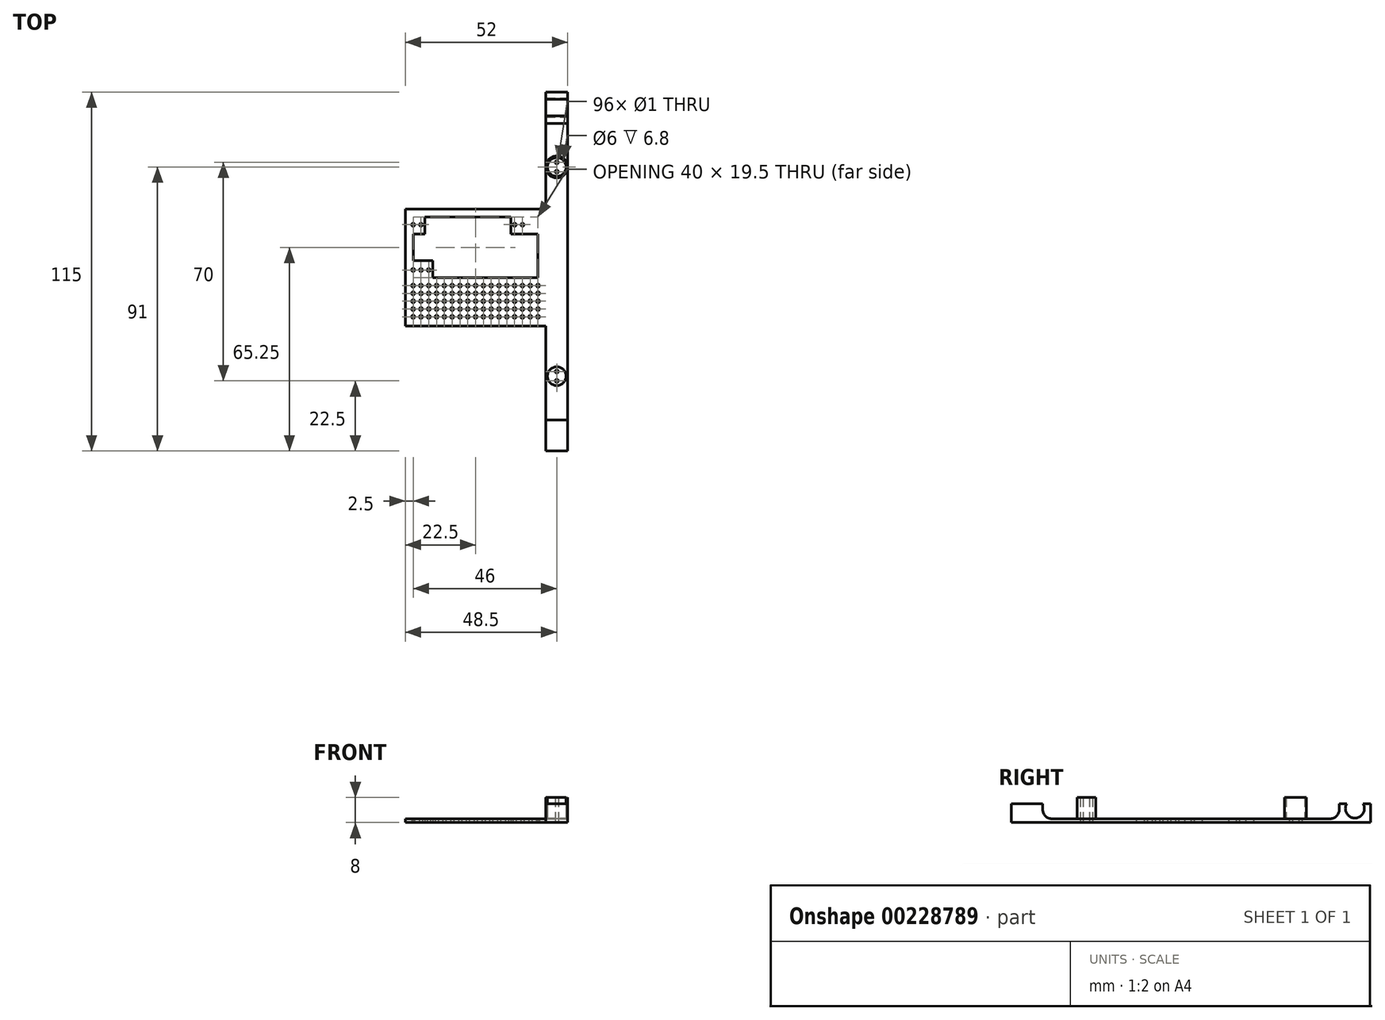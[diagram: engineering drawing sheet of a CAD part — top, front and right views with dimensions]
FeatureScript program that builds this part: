
annotation { "Feature Type Name" : "Feature", "Feature Type Description" : "" }
export const myFeature = defineFeature(function(context is Context, id is Id, definition is map)
    precondition{}
    {
        {
            var Q0;
            Q0=qCreatedBy(makeId("Top.planeOp"),FACE);
            var sketch = newSketch(context, id + "F0", { "sketchPlane" : qUnion([Q0])});
            skLineSegment(sketch, "E0.bottom", {"start": v(-22.5, 17.5) * mm, "end": v(22.5, 17.5) * mm});
            skLineSegment(sketch, "E0.top", {"start": v(-22.5, -17.5) * mm, "end": v(22.5, -17.5) * mm});
            skLineSegment(sketch, "E0.left", {"start": v(-22.5, 17.5) * mm, "end": v(-22.5, -17.5) * mm});
            skLineSegment(sketch, "E0.right", {"start": v(22.5, 17.5) * mm, "end": v(22.5, -17.5) * mm});
            skPoint(sketch, "E0.middle", {"position": v(0, 0) * mm});
            skCircle(sketch, "E1", {"center": v(-20, 15) * mm, "radius": 0.5 * mm});
            skLineSegment(sketch, "E2", {"start": v(-20, 15) * mm, "end": v(22.5, 15) * mm, "construction": true});
            skCircle(sketch, "E3.0.1.1", {"center": v(-20, 0.5) * mm, "radius": 0.5 * mm});
            skCircle(sketch, "E3.1.0.1", {"center": v(-17.5, 15) * mm, "radius": 0.5 * mm});
            skCircle(sketch, "E3.1.1.1", {"center": v(-17.5, 0.5) * mm, "radius": 0.5 * mm});
            skCircle(sketch, "E3.2.0.1", {"center": v(-15, 15) * mm, "radius": 0.5 * mm});
            skCircle(sketch, "E3.2.1.1", {"center": v(-15, 0.5) * mm, "radius": 0.5 * mm});
            skCircle(sketch, "E3.3.0.1", {"center": v(-12.5, 15) * mm, "radius": 0.5 * mm});
            skCircle(sketch, "E3.3.1.1", {"center": v(-12.5, 0.5) * mm, "radius": 0.5 * mm});
            skCircle(sketch, "E3.4.0.1", {"center": v(-10, 15) * mm, "radius": 0.5 * mm});
            skCircle(sketch, "E3.4.1.1", {"center": v(-10, 0.5) * mm, "radius": 0.5 * mm});
            skCircle(sketch, "E3.5.0.1", {"center": v(-7.5, 15) * mm, "radius": 0.5 * mm});
            skCircle(sketch, "E3.5.1.1", {"center": v(-7.5, 0.5) * mm, "radius": 0.5 * mm});
            skCircle(sketch, "E3.6.0.1", {"center": v(-5, 15) * mm, "radius": 0.5 * mm});
            skCircle(sketch, "E3.6.1.1", {"center": v(-5, 0.5) * mm, "radius": 0.5 * mm});
            skCircle(sketch, "E3.7.0.1", {"center": v(-2.5, 15) * mm, "radius": 0.5 * mm});
            skCircle(sketch, "E3.7.1.1", {"center": v(-2.5, 0.5) * mm, "radius": 0.5 * mm});
            skCircle(sketch, "E3.8.0.1", {"center": v(0, 15) * mm, "radius": 0.5 * mm});
            skCircle(sketch, "E3.8.1.1", {"center": v(0, 0.5) * mm, "radius": 0.5 * mm});
            skCircle(sketch, "E3.9.0.1", {"center": v(2.5, 15) * mm, "radius": 0.5 * mm});
            skCircle(sketch, "E3.9.1.1", {"center": v(2.5, 0.5) * mm, "radius": 0.5 * mm});
            skCircle(sketch, "E3.10.0.1", {"center": v(5, 15) * mm, "radius": 0.5 * mm});
            skCircle(sketch, "E3.10.1.1", {"center": v(5, 0.5) * mm, "radius": 0.5 * mm});
            skCircle(sketch, "E3.11.0.1", {"center": v(7.5, 15) * mm, "radius": 0.5 * mm});
            skCircle(sketch, "E3.11.1.1", {"center": v(7.5, 0.5) * mm, "radius": 0.5 * mm});
            skCircle(sketch, "E3.12.0.1", {"center": v(10, 15) * mm, "radius": 0.5 * mm});
            skCircle(sketch, "E3.12.1.1", {"center": v(10, 0.5) * mm, "radius": 0.5 * mm});
            skCircle(sketch, "E3.13.0.1", {"center": v(12.5, 15) * mm, "radius": 0.5 * mm});
            skCircle(sketch, "E3.13.1.1", {"center": v(12.5, 0.5) * mm, "radius": 0.5 * mm});
            skCircle(sketch, "E3.14.0.1", {"center": v(15, 15) * mm, "radius": 0.5 * mm});
            skCircle(sketch, "E3.14.1.1", {"center": v(15, 0.5) * mm, "radius": 0.5 * mm});
            skLineSegment(sketch, "E3.direction1", {"start": v(-20, 15) * mm, "end": v(-17.5, 15) * mm, "construction": true});
            skLineSegment(sketch, "E3.direction2", {"start": v(-20, 15) * mm, "end": v(-20, 0.5) * mm, "construction": true});
            skLineSegment(sketch, "E4", {"start": v(-22.5, -2) * mm, "end": v(22.5, -2) * mm, "construction": true});
            skCircle(sketch, "E5.MirrorC", {"center": v(-20, -4.5) * mm, "radius": 0.5 * mm});
            skCircle(sketch, "E6.0.1.0", {"center": v(-20, -7) * mm, "radius": 0.5 * mm});
            skCircle(sketch, "E6.0.2.0", {"center": v(-20, -9.5) * mm, "radius": 0.5 * mm});
            skCircle(sketch, "E6.0.3.0", {"center": v(-20, -12) * mm, "radius": 0.5 * mm});
            skCircle(sketch, "E6.1.0.0", {"center": v(-17.5, -4.5) * mm, "radius": 0.5 * mm});
            skCircle(sketch, "E6.1.1.0", {"center": v(-17.5, -7) * mm, "radius": 0.5 * mm});
            skCircle(sketch, "E6.1.2.0", {"center": v(-17.5, -9.5) * mm, "radius": 0.5 * mm});
            skCircle(sketch, "E6.1.3.0", {"center": v(-17.5, -12) * mm, "radius": 0.5 * mm});
            skCircle(sketch, "E6.2.0.0", {"center": v(-15, -4.5) * mm, "radius": 0.5 * mm});
            skCircle(sketch, "E6.2.1.0", {"center": v(-15, -7) * mm, "radius": 0.5 * mm});
            skCircle(sketch, "E6.2.2.0", {"center": v(-15, -9.5) * mm, "radius": 0.5 * mm});
            skCircle(sketch, "E6.2.3.0", {"center": v(-15, -12) * mm, "radius": 0.5 * mm});
            skCircle(sketch, "E6.3.0.0", {"center": v(-12.5, -4.5) * mm, "radius": 0.5 * mm});
            skCircle(sketch, "E6.3.1.0", {"center": v(-12.5, -7) * mm, "radius": 0.5 * mm});
            skCircle(sketch, "E6.3.2.0", {"center": v(-12.5, -9.5) * mm, "radius": 0.5 * mm});
            skCircle(sketch, "E6.3.3.0", {"center": v(-12.5, -12) * mm, "radius": 0.5 * mm});
            skCircle(sketch, "E6.4.0.0", {"center": v(-10, -4.5) * mm, "radius": 0.5 * mm});
            skCircle(sketch, "E6.4.1.0", {"center": v(-10, -7) * mm, "radius": 0.5 * mm});
            skCircle(sketch, "E6.4.2.0", {"center": v(-10, -9.5) * mm, "radius": 0.5 * mm});
            skCircle(sketch, "E6.4.3.0", {"center": v(-10, -12) * mm, "radius": 0.5 * mm});
            skCircle(sketch, "E6.5.0.0", {"center": v(-7.5, -4.5) * mm, "radius": 0.5 * mm});
            skCircle(sketch, "E6.5.1.0", {"center": v(-7.5, -7) * mm, "radius": 0.5 * mm});
            skCircle(sketch, "E6.5.2.0", {"center": v(-7.5, -9.5) * mm, "radius": 0.5 * mm});
            skCircle(sketch, "E6.5.3.0", {"center": v(-7.5, -12) * mm, "radius": 0.5 * mm});
            skCircle(sketch, "E6.6.0.0", {"center": v(-5, -4.5) * mm, "radius": 0.5 * mm});
            skCircle(sketch, "E6.6.1.0", {"center": v(-5, -7) * mm, "radius": 0.5 * mm});
            skCircle(sketch, "E6.6.2.0", {"center": v(-5, -9.5) * mm, "radius": 0.5 * mm});
            skCircle(sketch, "E6.6.3.0", {"center": v(-5, -12) * mm, "radius": 0.5 * mm});
            skCircle(sketch, "E6.7.0.0", {"center": v(-2.5, -4.5) * mm, "radius": 0.5 * mm});
            skCircle(sketch, "E6.7.1.0", {"center": v(-2.5, -7) * mm, "radius": 0.5 * mm});
            skCircle(sketch, "E6.7.2.0", {"center": v(-2.5, -9.5) * mm, "radius": 0.5 * mm});
            skCircle(sketch, "E6.7.3.0", {"center": v(-2.5, -12) * mm, "radius": 0.5 * mm});
            skCircle(sketch, "E6.8.0.0", {"center": v(0, -4.5) * mm, "radius": 0.5 * mm});
            skCircle(sketch, "E6.8.1.0", {"center": v(0, -7) * mm, "radius": 0.5 * mm});
            skCircle(sketch, "E6.8.2.0", {"center": v(0, -9.5) * mm, "radius": 0.5 * mm});
            skCircle(sketch, "E6.8.3.0", {"center": v(0, -12) * mm, "radius": 0.5 * mm});
            skCircle(sketch, "E6.9.0.0", {"center": v(2.5, -4.5) * mm, "radius": 0.5 * mm});
            skCircle(sketch, "E6.9.1.0", {"center": v(2.5, -7) * mm, "radius": 0.5 * mm});
            skCircle(sketch, "E6.9.2.0", {"center": v(2.5, -9.5) * mm, "radius": 0.5 * mm});
            skCircle(sketch, "E6.9.3.0", {"center": v(2.5, -12) * mm, "radius": 0.5 * mm});
            skCircle(sketch, "E6.10.0.0", {"center": v(5, -4.5) * mm, "radius": 0.5 * mm});
            skCircle(sketch, "E6.10.1.0", {"center": v(5, -7) * mm, "radius": 0.5 * mm});
            skCircle(sketch, "E6.10.2.0", {"center": v(5, -9.5) * mm, "radius": 0.5 * mm});
            skCircle(sketch, "E6.10.3.0", {"center": v(5, -12) * mm, "radius": 0.5 * mm});
            skCircle(sketch, "E6.11.0.0", {"center": v(7.5, -4.5) * mm, "radius": 0.5 * mm});
            skCircle(sketch, "E6.11.1.0", {"center": v(7.5, -7) * mm, "radius": 0.5 * mm});
            skCircle(sketch, "E6.11.2.0", {"center": v(7.5, -9.5) * mm, "radius": 0.5 * mm});
            skCircle(sketch, "E6.11.3.0", {"center": v(7.5, -12) * mm, "radius": 0.5 * mm});
            skCircle(sketch, "E6.12.0.0", {"center": v(10, -4.5) * mm, "radius": 0.5 * mm});
            skCircle(sketch, "E6.12.1.0", {"center": v(10, -7) * mm, "radius": 0.5 * mm});
            skCircle(sketch, "E6.12.2.0", {"center": v(10, -9.5) * mm, "radius": 0.5 * mm});
            skCircle(sketch, "E6.12.3.0", {"center": v(10, -12) * mm, "radius": 0.5 * mm});
            skCircle(sketch, "E6.13.0.0", {"center": v(12.5, -4.5) * mm, "radius": 0.5 * mm});
            skCircle(sketch, "E6.13.1.0", {"center": v(12.5, -7) * mm, "radius": 0.5 * mm});
            skCircle(sketch, "E6.13.2.0", {"center": v(12.5, -9.5) * mm, "radius": 0.5 * mm});
            skCircle(sketch, "E6.13.3.0", {"center": v(12.5, -12) * mm, "radius": 0.5 * mm});
            skCircle(sketch, "E6.14.0.0", {"center": v(15, -4.5) * mm, "radius": 0.5 * mm});
            skCircle(sketch, "E6.14.1.0", {"center": v(15, -7) * mm, "radius": 0.5 * mm});
            skCircle(sketch, "E6.14.2.0", {"center": v(15, -9.5) * mm, "radius": 0.5 * mm});
            skCircle(sketch, "E6.14.3.0", {"center": v(15, -12) * mm, "radius": 0.5 * mm});
            skLineSegment(sketch, "E6.direction1", {"start": v(-20, -4.5) * mm, "end": v(-17.5, -4.5) * mm, "construction": true});
            skLineSegment(sketch, "E6.direction2", {"start": v(-20, -4.5) * mm, "end": v(-20, -7) * mm, "construction": true});
            skCircle(sketch, "E7.0.15.0", {"center": v(17.5, -4.5) * mm, "radius": 0.5 * mm});
            skCircle(sketch, "E7.0.15.1", {"center": v(17.5, -7) * mm, "radius": 0.5 * mm});
            skCircle(sketch, "E7.0.15.2", {"center": v(17.5, -9.5) * mm, "radius": 0.5 * mm});
            skCircle(sketch, "E7.0.15.3", {"center": v(17.5, -12) * mm, "radius": 0.5 * mm});
            skCircle(sketch, "E8.0.16.0", {"center": v(20, -4.5) * mm, "radius": 0.5 * mm});
            skCircle(sketch, "E8.0.16.1", {"center": v(20, -7) * mm, "radius": 0.5 * mm});
            skCircle(sketch, "E8.0.16.2", {"center": v(20, -9.5) * mm, "radius": 0.5 * mm});
            skCircle(sketch, "E8.0.16.3", {"center": v(20, -12) * mm, "radius": 0.5 * mm});
            skCircle(sketch, "E9.0.0.4", {"center": v(-20, -14.5) * mm, "radius": 0.5 * mm});
            skCircle(sketch, "E9.0.1.4", {"center": v(-17.5, -14.5) * mm, "radius": 0.5 * mm});
            skCircle(sketch, "E9.0.2.4", {"center": v(-15, -14.5) * mm, "radius": 0.5 * mm});
            skCircle(sketch, "E9.0.3.4", {"center": v(-12.5, -14.5) * mm, "radius": 0.5 * mm});
            skCircle(sketch, "E9.0.4.4", {"center": v(-10, -14.5) * mm, "radius": 0.5 * mm});
            skCircle(sketch, "E9.0.5.4", {"center": v(-7.5, -14.5) * mm, "radius": 0.5 * mm});
            skCircle(sketch, "E9.0.6.4", {"center": v(-5, -14.5) * mm, "radius": 0.5 * mm});
            skCircle(sketch, "E9.0.7.4", {"center": v(-2.5, -14.5) * mm, "radius": 0.5 * mm});
            skCircle(sketch, "E9.0.8.4", {"center": v(0, -14.5) * mm, "radius": 0.5 * mm});
            skCircle(sketch, "E9.0.9.4", {"center": v(2.5, -14.5) * mm, "radius": 0.5 * mm});
            skCircle(sketch, "E9.0.10.4", {"center": v(5, -14.5) * mm, "radius": 0.5 * mm});
            skCircle(sketch, "E9.0.11.4", {"center": v(7.5, -14.5) * mm, "radius": 0.5 * mm});
            skCircle(sketch, "E9.0.12.4", {"center": v(10, -14.5) * mm, "radius": 0.5 * mm});
            skCircle(sketch, "E9.0.13.4", {"center": v(12.5, -14.5) * mm, "radius": 0.5 * mm});
            skCircle(sketch, "E9.0.14.4", {"center": v(15, -14.5) * mm, "radius": 0.5 * mm});
            skCircle(sketch, "E9.0.15.4", {"center": v(17.5, -14.5) * mm, "radius": 0.5 * mm});
            skCircle(sketch, "E9.0.16.4", {"center": v(20, -14.5) * mm, "radius": 0.5 * mm});
            skLineSegment(sketch, "E10.bottom", {"start": v(-20, 12) * mm, "end": v(20, 12) * mm});
            skLineSegment(sketch, "E10.top", {"start": v(-20, 3.5) * mm, "end": v(20, 3.5) * mm});
            skLineSegment(sketch, "E10.left", {"start": v(-20, 12) * mm, "end": v(-20, 3.5) * mm});
            skLineSegment(sketch, "E10.right", {"start": v(20, 12) * mm, "end": v(20, 3.5) * mm});
            skPoint(sketch, "E10.middle", {"position": v(0, 7.75) * mm});
            skLineSegment(sketch, "E11", {"start": v(22.5, 17.5) * mm, "end": v(22.5, 57.5) * mm});
            skLineSegment(sketch, "E12", {"start": v(22.5, 57.5) * mm, "end": v(29.5, 57.5) * mm});
            skLineSegment(sketch, "E13", {"start": v(29.5, -2) * mm, "end": v(22.5, -2) * mm, "construction": true});
            skLineSegment(sketch, "E14", {"start": v(29.5, 57.5) * mm, "end": v(29.5, -2) * mm});
            skLineSegment(sketch, "E15", {"start": v(22.5, 47.5) * mm, "end": v(29.5, 47.5) * mm});
            skLineSegment(sketch, "E16.MirrorCS", {"start": v(22.5, -47.5) * mm, "end": v(29.5, -47.5) * mm});
            skLineSegment(sketch, "E17.MirrorCS", {"start": v(29.5, -57.5) * mm, "end": v(29.5, 2) * mm});
            skLineSegment(sketch, "E18.MirrorCS", {"start": v(22.5, -17.5) * mm, "end": v(22.5, -57.5) * mm});
            skLineSegment(sketch, "E19.MirrorCS", {"start": v(22.5, -57.5) * mm, "end": v(29.5, -57.5) * mm});
            skCircle(sketch, "E20", {"center": v(26, 33.5) * mm, "radius": 3 * mm});
            skPoint(sketch, "E20.centerSnap0", {"position": v(26, 47.5) * mm});
            skCircle(sketch, "E21", {"center": v(26, 33.5) * mm, "radius": 3.5 * mm});
            skCircle(sketch, "E22.MirrorC", {"center": v(26, -33.5) * mm, "radius": 3 * mm});
            skCircle(sketch, "E23.MirrorC", {"center": v(26, -33.5) * mm, "radius": 3.5 * mm});
            skCircle(sketch, "E24", {"center": v(26, 35) * mm, "radius": 0.5 * mm});
            skCircle(sketch, "E25", {"center": v(26, 32) * mm, "radius": 0.5 * mm});
            skCircle(sketch, "E26.MirrorC", {"center": v(26, -35) * mm, "radius": 0.5 * mm});
            skCircle(sketch, "E27.MirrorC", {"center": v(26, -32) * mm, "radius": 0.5 * mm});
            skLineSegment(sketch, "E28", {"start": v(-13.75, 3.5) * mm, "end": v(-13.75, -2) * mm});
            skLineSegment(sketch, "E29", {"start": v(-13.75, -2) * mm, "end": v(20, -2) * mm});
            skLineSegment(sketch, "E30", {"start": v(20, -2) * mm, "end": v(20, 3.5) * mm});
            skLineSegment(sketch, "E31", {"start": v(11.25, 12) * mm, "end": v(11.25, 17.5) * mm});
            skLineSegment(sketch, "E32", {"start": v(-16.25, 17.5) * mm, "end": v(-16.25, 12) * mm});
            skLineSegment(sketch, "E33", {"start": v(-22.5, 17.5) * mm, "end": v(-22.5, 20) * mm});
            skLineSegment(sketch, "E34", {"start": v(-22.5, 20) * mm, "end": v(22.5, 20) * mm});
            skSolve(sketch);
        }
        {
            var Q0;
            Q0=makeQuery(id+"F0.imprint","IMPRINT",FACE,{"disambiguationData":[TD([[makeQuery(id+"F0.imprint","IMPRINT",EDGE,{"derivedFrom":sQuery(id+"F0.wireOp",EDGE,"E0.bottom")}),-1.0]])]});
            var Q1;
            {var subQ5=sQuery(id+"F0.wireOp",EDGE,"E0.right");Q1=makeQuery(id+"F0.imprint","IMPRINT",FACE,{"disambiguationData":[TD([[makeQuery(id+"F0.imprint","IMPRINT",EDGE,{"derivedFrom":subQ5}),1.0]])]});}
            var Q2;
            {var subQ0=sQuery(id+"F0.wireOp",EDGE,"E15");Q2=makeQuery(id+"F0.imprint","IMPRINT",FACE,{"disambiguationData":[TD([[makeQuery(id+"F0.imprint","IMPRINT",EDGE,{"derivedFrom":subQ0}),-1.0]])]});}
            var Q3;
            {var subQ0=sQuery(id+"F0.wireOp",EDGE,"E16.MirrorCS");Q3=makeQuery(id+"F0.imprint","IMPRINT",FACE,{"disambiguationData":[TD([[makeQuery(id+"F0.imprint","IMPRINT",EDGE,{"derivedFrom":subQ0}),1.0]])]});}
            var Q4;
            {var subQ0=sQuery(id+"F0.wireOp",EDGE,"E16.MirrorCS");Q4=makeQuery(id+"F0.imprint","IMPRINT",FACE,{"disambiguationData":[TD([[makeQuery(id+"F0.imprint","IMPRINT",EDGE,{"derivedFrom":subQ0}),-1.0]])]});}
            var Q5;
            {var subQ0=sQuery(id+"F0.wireOp",EDGE,"E12");Q5=makeQuery(id+"F0.imprint","IMPRINT",FACE,{"disambiguationData":[TD([[makeQuery(id+"F0.imprint","IMPRINT",EDGE,{"derivedFrom":subQ0}),-1.0]])]});}
            var Q6;
            Q6=makeQuery(id+"F0.imprint","IMPRINT",FACE,{"disambiguationData":[TD([[makeQuery(id+"F0.imprint","IMPRINT",EDGE,{"derivedFrom":sQuery(id+"F0.wireOp",EDGE,"E20")}),1.0]])]});
            var Q7;
            Q7=makeQuery(id+"F0.imprint","IMPRINT",FACE,{"disambiguationData":[TD([[makeQuery(id+"F0.imprint","IMPRINT",EDGE,{"derivedFrom":sQuery(id+"F0.wireOp",EDGE,"E22.MirrorC")}),-1.0]])]});
            var Q8;
            Q8=makeQuery(id+"F0.imprint","IMPRINT",FACE,{"disambiguationData":[TD([[makeQuery(id+"F0.imprint","IMPRINT",EDGE,{"derivedFrom":sQuery(id+"F0.wireOp",EDGE,"E20")}),-1.0]])]});
            var Q9;
            Q9=makeQuery(id+"F0.imprint","IMPRINT",FACE,{"disambiguationData":[TD([[makeQuery(id+"F0.imprint","IMPRINT",EDGE,{"derivedFrom":sQuery(id+"F0.wireOp",EDGE,"E22.MirrorC")}),1.0]])]});
            var Q10;
            {var subQ6=sQuery(id+"F0.wireOp",EDGE,"E33");Q10=makeQuery(id+"F0.imprint","IMPRINT",FACE,{"disambiguationData":[TD([[makeQuery(id+"F0.imprint","IMPRINT",EDGE,{"derivedFrom":subQ6}),-1.0]])]});}
            extrude(context, id + "F1", {"entities" : qUnion([Q0, Q1, Q2, Q3, Q4, Q5, Q6, Q7, Q8, Q9, Q10]), "depth" : 1.2 * mm});
        }
        {
            var Q0;
            {var subQ0=sQuery(id+"F0.wireOp",EDGE,"E12");Q0=makeQuery(id+"F0.imprint","IMPRINT",FACE,{"disambiguationData":[TD([[makeQuery(id+"F0.imprint","IMPRINT",EDGE,{"derivedFrom":subQ0}),-1.0]])]});}
            var Q1;
            {var subQ0=sQuery(id+"F0.wireOp",EDGE,"E16.MirrorCS");Q1=makeQuery(id+"F0.imprint","IMPRINT",FACE,{"disambiguationData":[TD([[makeQuery(id+"F0.imprint","IMPRINT",EDGE,{"derivedFrom":subQ0}),-1.0]])]});}
            extrude(context, id + "F2", {"entities" : qUnion([Q0, Q1]), "operationType" : NewBodyOperationType.ADD, "depth" : 6 * mm});
        }
        {
            var Q0;
            {var subQ0=sQuery(id+"F0.wireOp",EDGE,"E17.MirrorCS");var subQ1=sQuery(id+"F0.wireOp",EDGE,"E14");Q0=makeQuery(id+"F2.boolean.opBoolean","MERGE",FACE,{"derivedFrom":[makeQuery(id+"F1.opExtrude","SWEPT_FACE",FACE,{"disambiguationData":[OSD([subQ1,subQ0])]}),makeQuery(id+"F2.opExtrude","SWEPT_FACE",FACE,{"disambiguationData":[OSD([subQ1])]}),makeQuery(id+"F2.opExtrude","SWEPT_FACE",FACE,{"disambiguationData":[OSD([subQ0])]})]});}
            var sketch = newSketch(context, id + "F3", { "sketchPlane" : qUnion([Q0])});
            skCircle(sketch, "E35", {"center": v(52.5, 4.5) * mm, "radius": 3.05 * mm});
            skPoint(sketch, "E35.centerSnap0", {"position": v(52.5, 6) * mm});
            skCircle(sketch, "E36.MirrorC", {"center": v(-52.5, 4.5) * mm, "radius": 3.05 * mm});
            skSolve(sketch);
        }
        {
            var Q0;
            {var subQ0=sQuery(id+"F3.wireOp",EDGE,"E35");var subQ1=makeQuery(id+"F2.opExtrude","CAP_EDGE",EDGE,{"disambiguationData":[OSD([sQuery(id+"F0.wireOp",EDGE,"E14")])],"isStart":false});var subQ2=makeQuery(id+"F3.imprint","INTERSECT",VERTEX,{"disambiguationData":[OD(0.0)],"derivedFrom":[subQ1,subQ0]});Q0=makeQuery(id+"F3.imprint","IMPRINT",FACE,{"disambiguationData":[TD([[makeQuery(id+"F3.imprint","IMPRINT",EDGE,{"disambiguationData":[TD([[subQ2,1.0]])],"derivedFrom":subQ0}),1.0]])]});}
            var Q1;
            {var subQ0=sQuery(id+"F3.wireOp",EDGE,"E36.MirrorC");var subQ1=makeQuery(id+"F2.opExtrude","CAP_EDGE",EDGE,{"disambiguationData":[OSD([sQuery(id+"F0.wireOp",EDGE,"E17.MirrorCS")])],"isStart":false});var subQ2=makeQuery(id+"F3.imprint","INTERSECT",VERTEX,{"disambiguationData":[OD(0.0)],"derivedFrom":[subQ1,subQ0]});Q1=makeQuery(id+"F3.imprint","IMPRINT",FACE,{"disambiguationData":[TD([[makeQuery(id+"F3.imprint","IMPRINT",EDGE,{"disambiguationData":[TD([[subQ2,-1.0]])],"derivedFrom":subQ0}),-1.0]])]});}
            extrude(context, id + "F4", {"entities" : qUnion([Q0, Q1]), "operationType" : NewBodyOperationType.REMOVE, "oppositeDirection" : true, "depth" : 25 * mm});
        }
        {
            var Q0;
            Q0=makeQuery(id+"F0.imprint","IMPRINT",FACE,{"disambiguationData":[TD([[makeQuery(id+"F0.imprint","IMPRINT",EDGE,{"derivedFrom":sQuery(id+"F0.wireOp",EDGE,"E20")}),-1.0]])]});
            var Q1;
            Q1=makeQuery(id+"F0.imprint","IMPRINT",FACE,{"disambiguationData":[TD([[makeQuery(id+"F0.imprint","IMPRINT",EDGE,{"derivedFrom":sQuery(id+"F0.wireOp",EDGE,"E22.MirrorC")}),1.0]])]});
            extrude(context, id + "F5", {"entities" : qUnion([Q0, Q1]), "operationType" : NewBodyOperationType.ADD, "depth" : 8 * mm});
        }
        {
            var Q0;
            Q0=makeQuery(id+"F2.boolean.opBoolean","INTERSECT",EDGE,{"derivedFrom":[makeQuery(id+"F1.opExtrude","CAP_FACE",FACE,{"disambiguationData":[OSD([sQuery(id+"F0.wireOp",EDGE,"E0.bottom"),sQuery(id+"F0.wireOp",EDGE,"E0.top"),sQuery(id+"F0.wireOp",EDGE,"E0.left"),sQuery(id+"F0.wireOp",EDGE,"E1"),sQuery(id+"F0.wireOp",EDGE,"E3.0.1.1"),sQuery(id+"F0.wireOp",EDGE,"E3.1.0.1"),sQuery(id+"F0.wireOp",EDGE,"E3.1.1.1"),sQuery(id+"F0.wireOp",EDGE,"E3.2.0.1"),sQuery(id+"F0.wireOp",EDGE,"E3.2.1.1"),sQuery(id+"F0.wireOp",EDGE,"E3.3.0.1"),sQuery(id+"F0.wireOp",EDGE,"E3.3.1.1"),sQuery(id+"F0.wireOp",EDGE,"E3.4.0.1"),sQuery(id+"F0.wireOp",EDGE,"E3.4.1.1"),sQuery(id+"F0.wireOp",EDGE,"E3.5.0.1"),sQuery(id+"F0.wireOp",EDGE,"E3.5.1.1"),sQuery(id+"F0.wireOp",EDGE,"E3.6.0.1"),sQuery(id+"F0.wireOp",EDGE,"E3.6.1.1"),sQuery(id+"F0.wireOp",EDGE,"E3.7.0.1"),sQuery(id+"F0.wireOp",EDGE,"E3.7.1.1"),sQuery(id+"F0.wireOp",EDGE,"E3.8.0.1"),sQuery(id+"F0.wireOp",EDGE,"E3.8.1.1"),sQuery(id+"F0.wireOp",EDGE,"E3.9.0.1"),sQuery(id+"F0.wireOp",EDGE,"E3.9.1.1"),sQuery(id+"F0.wireOp",EDGE,"E3.10.0.1"),sQuery(id+"F0.wireOp",EDGE,"E3.10.1.1"),sQuery(id+"F0.wireOp",EDGE,"E3.11.0.1"),sQuery(id+"F0.wireOp",EDGE,"E3.11.1.1"),sQuery(id+"F0.wireOp",EDGE,"E3.12.0.1"),sQuery(id+"F0.wireOp",EDGE,"E3.12.1.1"),sQuery(id+"F0.wireOp",EDGE,"E3.13.0.1"),sQuery(id+"F0.wireOp",EDGE,"E3.13.1.1"),sQuery(id+"F0.wireOp",EDGE,"E3.14.0.1"),sQuery(id+"F0.wireOp",EDGE,"E3.14.1.1"),sQuery(id+"F0.wireOp",EDGE,"E5.MirrorC"),sQuery(id+"F0.wireOp",EDGE,"E6.0.1.0"),sQuery(id+"F0.wireOp",EDGE,"E6.0.2.0"),sQuery(id+"F0.wireOp",EDGE,"E6.0.3.0"),sQuery(id+"F0.wireOp",EDGE,"E6.1.0.0"),sQuery(id+"F0.wireOp",EDGE,"E6.1.1.0"),sQuery(id+"F0.wireOp",EDGE,"E6.1.2.0"),sQuery(id+"F0.wireOp",EDGE,"E6.1.3.0"),sQuery(id+"F0.wireOp",EDGE,"E6.2.0.0"),sQuery(id+"F0.wireOp",EDGE,"E6.2.1.0"),sQuery(id+"F0.wireOp",EDGE,"E6.2.2.0"),sQuery(id+"F0.wireOp",EDGE,"E6.2.3.0"),sQuery(id+"F0.wireOp",EDGE,"E6.3.0.0"),sQuery(id+"F0.wireOp",EDGE,"E6.3.1.0"),sQuery(id+"F0.wireOp",EDGE,"E6.3.2.0"),sQuery(id+"F0.wireOp",EDGE,"E6.3.3.0"),sQuery(id+"F0.wireOp",EDGE,"E6.4.0.0"),sQuery(id+"F0.wireOp",EDGE,"E6.4.1.0"),sQuery(id+"F0.wireOp",EDGE,"E6.4.2.0"),sQuery(id+"F0.wireOp",EDGE,"E6.4.3.0"),sQuery(id+"F0.wireOp",EDGE,"E6.5.0.0"),sQuery(id+"F0.wireOp",EDGE,"E6.5.1.0"),sQuery(id+"F0.wireOp",EDGE,"E6.5.2.0"),sQuery(id+"F0.wireOp",EDGE,"E6.5.3.0"),sQuery(id+"F0.wireOp",EDGE,"E6.6.0.0"),sQuery(id+"F0.wireOp",EDGE,"E6.6.1.0"),sQuery(id+"F0.wireOp",EDGE,"E6.6.2.0"),sQuery(id+"F0.wireOp",EDGE,"E6.6.3.0"),sQuery(id+"F0.wireOp",EDGE,"E6.7.0.0"),sQuery(id+"F0.wireOp",EDGE,"E6.7.1.0"),sQuery(id+"F0.wireOp",EDGE,"E6.7.2.0"),sQuery(id+"F0.wireOp",EDGE,"E6.7.3.0"),sQuery(id+"F0.wireOp",EDGE,"E6.8.0.0"),sQuery(id+"F0.wireOp",EDGE,"E6.8.1.0"),sQuery(id+"F0.wireOp",EDGE,"E6.8.2.0"),sQuery(id+"F0.wireOp",EDGE,"E6.8.3.0"),sQuery(id+"F0.wireOp",EDGE,"E6.9.0.0"),sQuery(id+"F0.wireOp",EDGE,"E6.9.1.0"),sQuery(id+"F0.wireOp",EDGE,"E6.9.2.0"),sQuery(id+"F0.wireOp",EDGE,"E6.9.3.0"),sQuery(id+"F0.wireOp",EDGE,"E6.10.0.0"),sQuery(id+"F0.wireOp",EDGE,"E6.10.1.0"),sQuery(id+"F0.wireOp",EDGE,"E6.10.2.0"),sQuery(id+"F0.wireOp",EDGE,"E6.10.3.0"),sQuery(id+"F0.wireOp",EDGE,"E6.11.0.0"),sQuery(id+"F0.wireOp",EDGE,"E6.11.1.0"),sQuery(id+"F0.wireOp",EDGE,"E6.11.2.0"),sQuery(id+"F0.wireOp",EDGE,"E6.11.3.0"),sQuery(id+"F0.wireOp",EDGE,"E6.12.0.0"),sQuery(id+"F0.wireOp",EDGE,"E6.12.1.0"),sQuery(id+"F0.wireOp",EDGE,"E6.12.2.0"),sQuery(id+"F0.wireOp",EDGE,"E6.12.3.0"),sQuery(id+"F0.wireOp",EDGE,"E6.13.0.0"),sQuery(id+"F0.wireOp",EDGE,"E6.13.1.0"),sQuery(id+"F0.wireOp",EDGE,"E6.13.2.0"),sQuery(id+"F0.wireOp",EDGE,"E6.13.3.0"),sQuery(id+"F0.wireOp",EDGE,"E6.14.0.0"),sQuery(id+"F0.wireOp",EDGE,"E6.14.1.0"),sQuery(id+"F0.wireOp",EDGE,"E6.14.2.0"),sQuery(id+"F0.wireOp",EDGE,"E6.14.3.0"),sQuery(id+"F0.wireOp",EDGE,"E7.0.15.0"),sQuery(id+"F0.wireOp",EDGE,"E7.0.15.1"),sQuery(id+"F0.wireOp",EDGE,"E7.0.15.2"),sQuery(id+"F0.wireOp",EDGE,"E7.0.15.3"),sQuery(id+"F0.wireOp",EDGE,"E8.0.16.0"),sQuery(id+"F0.wireOp",EDGE,"E8.0.16.1"),sQuery(id+"F0.wireOp",EDGE,"E8.0.16.2"),sQuery(id+"F0.wireOp",EDGE,"E8.0.16.3"),sQuery(id+"F0.wireOp",EDGE,"E9.0.0.4"),sQuery(id+"F0.wireOp",EDGE,"E9.0.1.4"),sQuery(id+"F0.wireOp",EDGE,"E9.0.2.4"),sQuery(id+"F0.wireOp",EDGE,"E9.0.3.4"),sQuery(id+"F0.wireOp",EDGE,"E9.0.4.4"),sQuery(id+"F0.wireOp",EDGE,"E9.0.5.4"),sQuery(id+"F0.wireOp",EDGE,"E9.0.6.4"),sQuery(id+"F0.wireOp",EDGE,"E9.0.7.4"),sQuery(id+"F0.wireOp",EDGE,"E9.0.8.4"),sQuery(id+"F0.wireOp",EDGE,"E9.0.9.4"),sQuery(id+"F0.wireOp",EDGE,"E9.0.10.4"),sQuery(id+"F0.wireOp",EDGE,"E9.0.11.4"),sQuery(id+"F0.wireOp",EDGE,"E9.0.12.4"),sQuery(id+"F0.wireOp",EDGE,"E9.0.13.4"),sQuery(id+"F0.wireOp",EDGE,"E9.0.14.4"),sQuery(id+"F0.wireOp",EDGE,"E9.0.15.4"),sQuery(id+"F0.wireOp",EDGE,"E9.0.16.4"),sQuery(id+"F0.wireOp",EDGE,"E10.bottom"),sQuery(id+"F0.wireOp",EDGE,"E10.top"),sQuery(id+"F0.wireOp",EDGE,"E10.left"),sQuery(id+"F0.wireOp",EDGE,"E10.right"),sQuery(id+"F0.wireOp",EDGE,"E11"),sQuery(id+"F0.wireOp",EDGE,"E12"),sQuery(id+"F0.wireOp",EDGE,"E14"),sQuery(id+"F0.wireOp",EDGE,"E17.MirrorCS"),sQuery(id+"F0.wireOp",EDGE,"E18.MirrorCS"),sQuery(id+"F0.wireOp",EDGE,"E19.MirrorCS"),sQuery(id+"F0.wireOp",EDGE,"E24"),sQuery(id+"F0.wireOp",EDGE,"E25"),sQuery(id+"F0.wireOp",EDGE,"E26.MirrorC"),sQuery(id+"F0.wireOp",EDGE,"E27.MirrorC")])],"isStart":false}),makeQuery(id+"F2.opExtrude","SWEPT_FACE",FACE,{"disambiguationData":[OSD([sQuery(id+"F0.wireOp",EDGE,"E15")])]})]});
            fillet(context, id + "F6", {"entities" : qUnion([Q0]), "radius" : 3 * mm, "tangentPropagation" : true, "allowEdgeOverflow" : false});
        }
        {
            var Q0;
            Q0=makeQuery(id+"F2.boolean.opBoolean","INTERSECT",EDGE,{"derivedFrom":[makeQuery(id+"F1.opExtrude","CAP_FACE",FACE,{"disambiguationData":[OSD([sQuery(id+"F0.wireOp",EDGE,"E0.bottom"),sQuery(id+"F0.wireOp",EDGE,"E0.top"),sQuery(id+"F0.wireOp",EDGE,"E0.left"),sQuery(id+"F0.wireOp",EDGE,"E1"),sQuery(id+"F0.wireOp",EDGE,"E3.0.1.1"),sQuery(id+"F0.wireOp",EDGE,"E3.1.0.1"),sQuery(id+"F0.wireOp",EDGE,"E3.1.1.1"),sQuery(id+"F0.wireOp",EDGE,"E3.2.0.1"),sQuery(id+"F0.wireOp",EDGE,"E3.2.1.1"),sQuery(id+"F0.wireOp",EDGE,"E3.3.0.1"),sQuery(id+"F0.wireOp",EDGE,"E3.3.1.1"),sQuery(id+"F0.wireOp",EDGE,"E3.4.0.1"),sQuery(id+"F0.wireOp",EDGE,"E3.4.1.1"),sQuery(id+"F0.wireOp",EDGE,"E3.5.0.1"),sQuery(id+"F0.wireOp",EDGE,"E3.5.1.1"),sQuery(id+"F0.wireOp",EDGE,"E3.6.0.1"),sQuery(id+"F0.wireOp",EDGE,"E3.6.1.1"),sQuery(id+"F0.wireOp",EDGE,"E3.7.0.1"),sQuery(id+"F0.wireOp",EDGE,"E3.7.1.1"),sQuery(id+"F0.wireOp",EDGE,"E3.8.0.1"),sQuery(id+"F0.wireOp",EDGE,"E3.8.1.1"),sQuery(id+"F0.wireOp",EDGE,"E3.9.0.1"),sQuery(id+"F0.wireOp",EDGE,"E3.9.1.1"),sQuery(id+"F0.wireOp",EDGE,"E3.10.0.1"),sQuery(id+"F0.wireOp",EDGE,"E3.10.1.1"),sQuery(id+"F0.wireOp",EDGE,"E3.11.0.1"),sQuery(id+"F0.wireOp",EDGE,"E3.11.1.1"),sQuery(id+"F0.wireOp",EDGE,"E3.12.0.1"),sQuery(id+"F0.wireOp",EDGE,"E3.12.1.1"),sQuery(id+"F0.wireOp",EDGE,"E3.13.0.1"),sQuery(id+"F0.wireOp",EDGE,"E3.13.1.1"),sQuery(id+"F0.wireOp",EDGE,"E3.14.0.1"),sQuery(id+"F0.wireOp",EDGE,"E3.14.1.1"),sQuery(id+"F0.wireOp",EDGE,"E5.MirrorC"),sQuery(id+"F0.wireOp",EDGE,"E6.0.1.0"),sQuery(id+"F0.wireOp",EDGE,"E6.0.2.0"),sQuery(id+"F0.wireOp",EDGE,"E6.0.3.0"),sQuery(id+"F0.wireOp",EDGE,"E6.1.0.0"),sQuery(id+"F0.wireOp",EDGE,"E6.1.1.0"),sQuery(id+"F0.wireOp",EDGE,"E6.1.2.0"),sQuery(id+"F0.wireOp",EDGE,"E6.1.3.0"),sQuery(id+"F0.wireOp",EDGE,"E6.2.0.0"),sQuery(id+"F0.wireOp",EDGE,"E6.2.1.0"),sQuery(id+"F0.wireOp",EDGE,"E6.2.2.0"),sQuery(id+"F0.wireOp",EDGE,"E6.2.3.0"),sQuery(id+"F0.wireOp",EDGE,"E6.3.0.0"),sQuery(id+"F0.wireOp",EDGE,"E6.3.1.0"),sQuery(id+"F0.wireOp",EDGE,"E6.3.2.0"),sQuery(id+"F0.wireOp",EDGE,"E6.3.3.0"),sQuery(id+"F0.wireOp",EDGE,"E6.4.0.0"),sQuery(id+"F0.wireOp",EDGE,"E6.4.1.0"),sQuery(id+"F0.wireOp",EDGE,"E6.4.2.0"),sQuery(id+"F0.wireOp",EDGE,"E6.4.3.0"),sQuery(id+"F0.wireOp",EDGE,"E6.5.0.0"),sQuery(id+"F0.wireOp",EDGE,"E6.5.1.0"),sQuery(id+"F0.wireOp",EDGE,"E6.5.2.0"),sQuery(id+"F0.wireOp",EDGE,"E6.5.3.0"),sQuery(id+"F0.wireOp",EDGE,"E6.6.0.0"),sQuery(id+"F0.wireOp",EDGE,"E6.6.1.0"),sQuery(id+"F0.wireOp",EDGE,"E6.6.2.0"),sQuery(id+"F0.wireOp",EDGE,"E6.6.3.0"),sQuery(id+"F0.wireOp",EDGE,"E6.7.0.0"),sQuery(id+"F0.wireOp",EDGE,"E6.7.1.0"),sQuery(id+"F0.wireOp",EDGE,"E6.7.2.0"),sQuery(id+"F0.wireOp",EDGE,"E6.7.3.0"),sQuery(id+"F0.wireOp",EDGE,"E6.8.0.0"),sQuery(id+"F0.wireOp",EDGE,"E6.8.1.0"),sQuery(id+"F0.wireOp",EDGE,"E6.8.2.0"),sQuery(id+"F0.wireOp",EDGE,"E6.8.3.0"),sQuery(id+"F0.wireOp",EDGE,"E6.9.0.0"),sQuery(id+"F0.wireOp",EDGE,"E6.9.1.0"),sQuery(id+"F0.wireOp",EDGE,"E6.9.2.0"),sQuery(id+"F0.wireOp",EDGE,"E6.9.3.0"),sQuery(id+"F0.wireOp",EDGE,"E6.10.0.0"),sQuery(id+"F0.wireOp",EDGE,"E6.10.1.0"),sQuery(id+"F0.wireOp",EDGE,"E6.10.2.0"),sQuery(id+"F0.wireOp",EDGE,"E6.10.3.0"),sQuery(id+"F0.wireOp",EDGE,"E6.11.0.0"),sQuery(id+"F0.wireOp",EDGE,"E6.11.1.0"),sQuery(id+"F0.wireOp",EDGE,"E6.11.2.0"),sQuery(id+"F0.wireOp",EDGE,"E6.11.3.0"),sQuery(id+"F0.wireOp",EDGE,"E6.12.0.0"),sQuery(id+"F0.wireOp",EDGE,"E6.12.1.0"),sQuery(id+"F0.wireOp",EDGE,"E6.12.2.0"),sQuery(id+"F0.wireOp",EDGE,"E6.12.3.0"),sQuery(id+"F0.wireOp",EDGE,"E6.13.0.0"),sQuery(id+"F0.wireOp",EDGE,"E6.13.1.0"),sQuery(id+"F0.wireOp",EDGE,"E6.13.2.0"),sQuery(id+"F0.wireOp",EDGE,"E6.13.3.0"),sQuery(id+"F0.wireOp",EDGE,"E6.14.0.0"),sQuery(id+"F0.wireOp",EDGE,"E6.14.1.0"),sQuery(id+"F0.wireOp",EDGE,"E6.14.2.0"),sQuery(id+"F0.wireOp",EDGE,"E6.14.3.0"),sQuery(id+"F0.wireOp",EDGE,"E7.0.15.0"),sQuery(id+"F0.wireOp",EDGE,"E7.0.15.1"),sQuery(id+"F0.wireOp",EDGE,"E7.0.15.2"),sQuery(id+"F0.wireOp",EDGE,"E7.0.15.3"),sQuery(id+"F0.wireOp",EDGE,"E8.0.16.0"),sQuery(id+"F0.wireOp",EDGE,"E8.0.16.1"),sQuery(id+"F0.wireOp",EDGE,"E8.0.16.2"),sQuery(id+"F0.wireOp",EDGE,"E8.0.16.3"),sQuery(id+"F0.wireOp",EDGE,"E9.0.0.4"),sQuery(id+"F0.wireOp",EDGE,"E9.0.1.4"),sQuery(id+"F0.wireOp",EDGE,"E9.0.2.4"),sQuery(id+"F0.wireOp",EDGE,"E9.0.3.4"),sQuery(id+"F0.wireOp",EDGE,"E9.0.4.4"),sQuery(id+"F0.wireOp",EDGE,"E9.0.5.4"),sQuery(id+"F0.wireOp",EDGE,"E9.0.6.4"),sQuery(id+"F0.wireOp",EDGE,"E9.0.7.4"),sQuery(id+"F0.wireOp",EDGE,"E9.0.8.4"),sQuery(id+"F0.wireOp",EDGE,"E9.0.9.4"),sQuery(id+"F0.wireOp",EDGE,"E9.0.10.4"),sQuery(id+"F0.wireOp",EDGE,"E9.0.11.4"),sQuery(id+"F0.wireOp",EDGE,"E9.0.12.4"),sQuery(id+"F0.wireOp",EDGE,"E9.0.13.4"),sQuery(id+"F0.wireOp",EDGE,"E9.0.14.4"),sQuery(id+"F0.wireOp",EDGE,"E9.0.15.4"),sQuery(id+"F0.wireOp",EDGE,"E9.0.16.4"),sQuery(id+"F0.wireOp",EDGE,"E10.bottom"),sQuery(id+"F0.wireOp",EDGE,"E10.top"),sQuery(id+"F0.wireOp",EDGE,"E10.left"),sQuery(id+"F0.wireOp",EDGE,"E10.right"),sQuery(id+"F0.wireOp",EDGE,"E11"),sQuery(id+"F0.wireOp",EDGE,"E12"),sQuery(id+"F0.wireOp",EDGE,"E14"),sQuery(id+"F0.wireOp",EDGE,"E17.MirrorCS"),sQuery(id+"F0.wireOp",EDGE,"E18.MirrorCS"),sQuery(id+"F0.wireOp",EDGE,"E19.MirrorCS"),sQuery(id+"F0.wireOp",EDGE,"E24"),sQuery(id+"F0.wireOp",EDGE,"E25"),sQuery(id+"F0.wireOp",EDGE,"E26.MirrorC"),sQuery(id+"F0.wireOp",EDGE,"E27.MirrorC")])],"isStart":false}),makeQuery(id+"F2.opExtrude","SWEPT_FACE",FACE,{"disambiguationData":[OSD([sQuery(id+"F0.wireOp",EDGE,"E16.MirrorCS")])]})]});
            fillet(context, id + "F7", {"entities" : qUnion([Q0]), "radius" : 3 * mm, "tangentPropagation" : true, "allowEdgeOverflow" : false});
        }
    });
